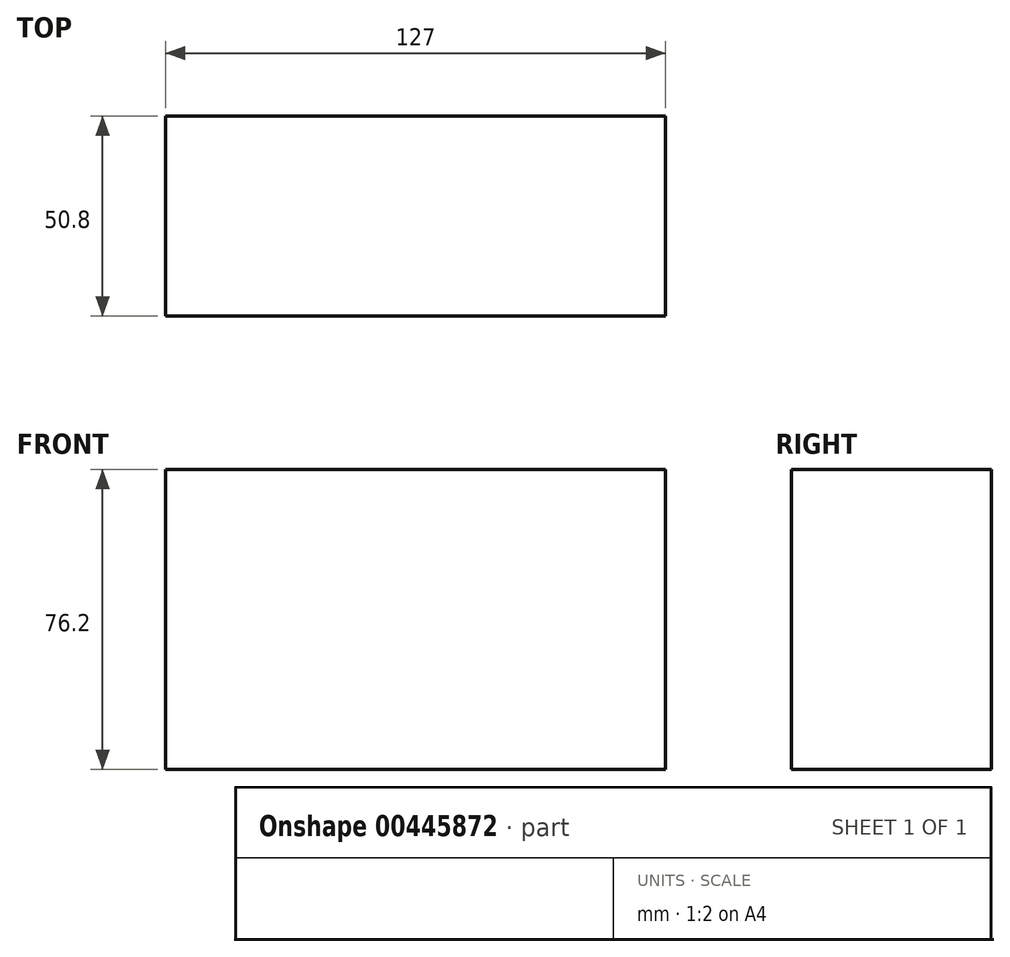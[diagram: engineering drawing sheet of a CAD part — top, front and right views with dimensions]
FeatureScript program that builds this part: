
annotation { "Feature Type Name" : "Feature", "Feature Type Description" : "" }
export const myFeature = defineFeature(function(context is Context, id is Id, definition is map)
    precondition{}
    {
        {
            var Q0;
            Q0=qCreatedBy(makeId("Front.planeOp"),FACE);
            var sketch = newSketch(context, id + "F0", { "sketchPlane" : qUnion([Q0])});
            skLineSegment(sketch, "E0.bottom", {"start": v(-68.81, 26.65) * mm, "end": v(58.19, 26.65) * mm});
            skLineSegment(sketch, "E0.top", {"start": v(-68.81, -49.55) * mm, "end": v(58.19, -49.55) * mm});
            skLineSegment(sketch, "E0.left", {"start": v(-68.81, 26.65) * mm, "end": v(-68.81, -49.55) * mm});
            skLineSegment(sketch, "E0.right", {"start": v(58.19, 26.65) * mm, "end": v(58.19, -49.55) * mm});
            skSolve(sketch);
        }
        {
            var Q0;
            Q0=makeQuery(id+"F0.imprint","IMPRINT",FACE,{"disambiguationData":[TD([[makeQuery(id+"F0.imprint","IMPRINT",EDGE,{"derivedFrom":sQuery(id+"F0.wireOp",EDGE,"E0.bottom")}),-1.0]])]});
            extrude(context, id + "F1", {"entities" : qUnion([Q0]), "depth" : 50.8 * mm});
        }
    });
